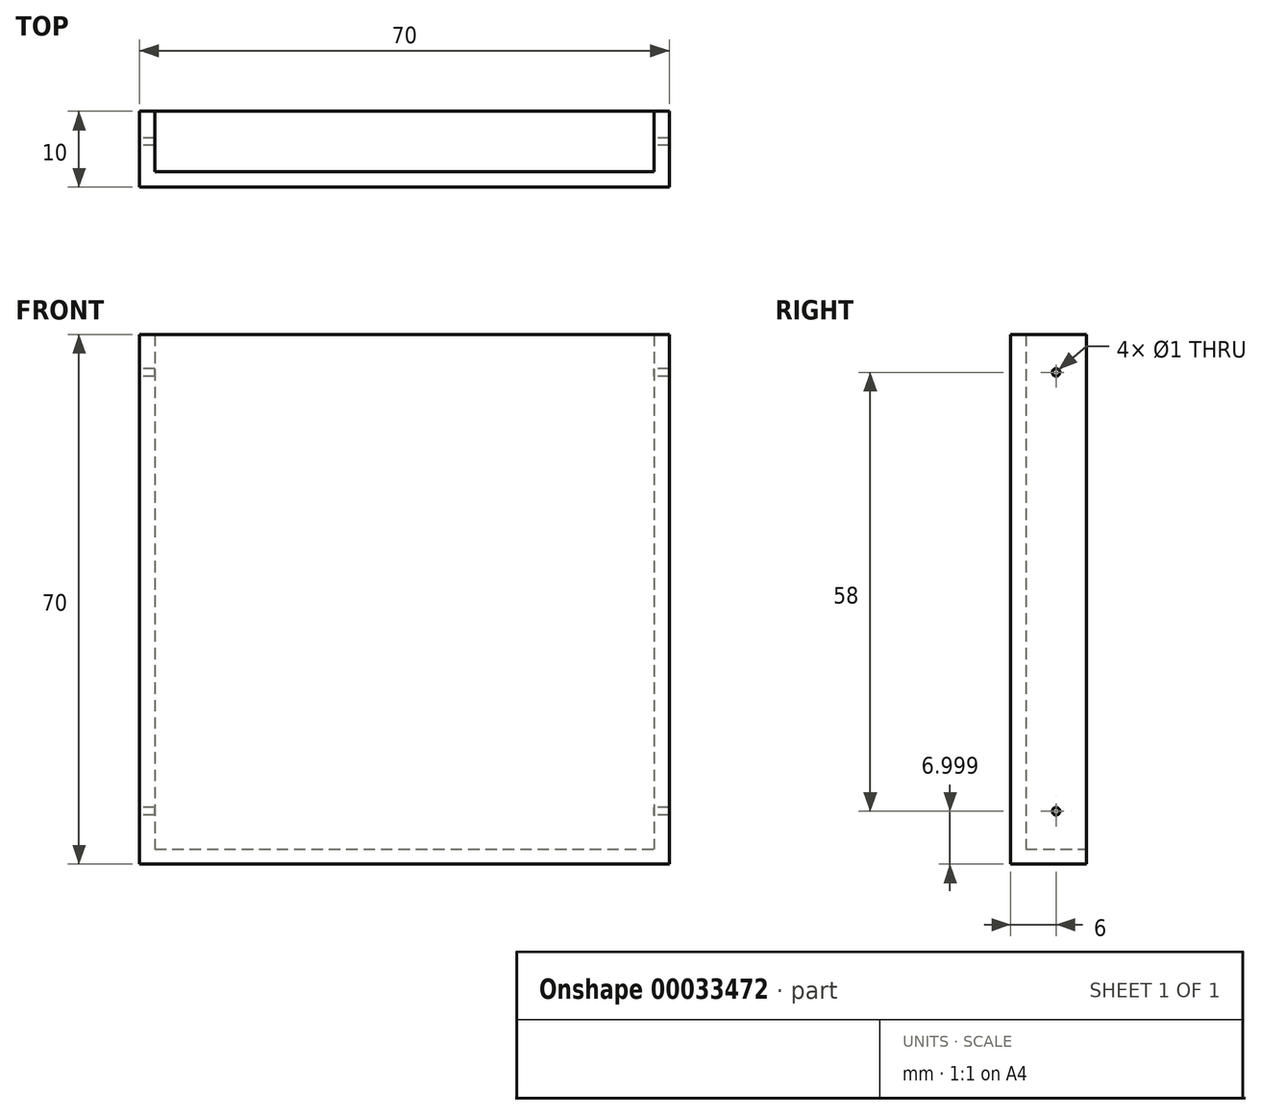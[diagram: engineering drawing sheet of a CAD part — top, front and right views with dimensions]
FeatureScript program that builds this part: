
annotation { "Feature Type Name" : "Feature", "Feature Type Description" : "" }
export const myFeature = defineFeature(function(context is Context, id is Id, definition is map)
    precondition{}
    {
        {
            var Q0;
            Q0=qCreatedBy(makeId("Front.planeOp"),FACE);
            var sketch = newSketch(context, id + "F0", { "sketchPlane" : qUnion([Q0])});
            skLineSegment(sketch, "E0.bottom", {"start": v(-35, 27.79) * mm, "end": v(35, 27.79) * mm});
            skLineSegment(sketch, "E0.top", {"start": v(-35, -42.21) * mm, "end": v(35, -42.21) * mm});
            skLineSegment(sketch, "E0.left", {"start": v(-35, 27.79) * mm, "end": v(-35, -42.21) * mm});
            skLineSegment(sketch, "E0.right", {"start": v(35, 27.79) * mm, "end": v(35, -42.21) * mm});
            skLineSegment(sketch, "E1", {"start": v(0, 0) * mm, "end": v(0, 74.16) * mm, "construction": true});
            skSolve(sketch);
        }
        {
            var Q0;
            Q0=makeQuery(id+"F0.imprint","IMPRINT",FACE,{"disambiguationData":[TD([[makeQuery(id+"F0.imprint","IMPRINT",EDGE,{"derivedFrom":sQuery(id+"F0.wireOp",EDGE,"E0.bottom")}),-1.0]])]});
            extrude(context, id + "F1", {"entities" : qUnion([Q0]), "depth" : 10 * mm});
        }
        {
            var Q0;
            Q0=makeQuery(id+"F1.opExtrude","CAP_FACE",FACE,{"disambiguationData":[OSD([sQuery(id+"F0.wireOp",EDGE,"E0.bottom"),sQuery(id+"F0.wireOp",EDGE,"E0.top"),sQuery(id+"F0.wireOp",EDGE,"E0.left"),sQuery(id+"F0.wireOp",EDGE,"E0.right")])],"isStart":true});
            shell(context, id + "F2", {"entities" : qUnion([Q0]), "thickness" : 2 * mm});
        }
        {
            var Q0;
            Q0=makeQuery(id+"F1.opExtrude","SWEPT_FACE",FACE,{"disambiguationData":[OSD([sQuery(id+"F0.wireOp",EDGE,"E0.bottom")])]});
            var sketch = newSketch(context, id + "F3", { "sketchPlane" : qUnion([Q0])});
            skLineSegment(sketch, "E2", {"start": v(-33, 0) * mm, "end": v(-33, -8) * mm});
            skLineSegment(sketch, "E3", {"start": v(-33, -8) * mm, "end": v(33, -8) * mm});
            skLineSegment(sketch, "E4", {"start": v(33, -8) * mm, "end": v(33, 0) * mm});
            skSolve(sketch);
        }
        {
            var Q0;
            {var subQ2=sQuery(id+"F3.wireOp",EDGE,"E2");Q0=makeQuery(id+"F3.imprint","IMPRINT",FACE,{"disambiguationData":[TD([[makeQuery(id+"F3.imprint","IMPRINT",EDGE,{"derivedFrom":subQ2}),1.0]])]});}
            extrude(context, id + "F4", {"entities" : qUnion([Q0]), "operationType" : NewBodyOperationType.REMOVE, "oppositeDirection" : true, "depth" : 4.33 * mm});
        }
        {
            var Q0;
            Q0=makeQuery(id+"F4.boolean.opBoolean","MERGE",FACE,{"derivedFrom":[makeQuery(id+"F2.opShell","OFFSET_FACE",FACE,{"disambiguationData":[OSD([sQuery(id+"F0.wireOp",EDGE,"E0.right")])]}),makeQuery(id+"F4.opExtrude","SWEPT_FACE",FACE,{"disambiguationData":[OSD([sQuery(id+"F3.wireOp",EDGE,"E4")])]})]});
            var sketch = newSketch(context, id + "F5", { "sketchPlane" : qUnion([Q0])});
            skCircle(sketch, "E5", {"center": v(4, 22.79) * mm, "radius": 0.5 * mm});
            skCircle(sketch, "E6", {"center": v(4, -35.21) * mm, "radius": 0.5 * mm});
            skLineSegment(sketch, "E7", {"start": v(4, 27.79) * mm, "end": v(4, -40.21) * mm, "construction": true});
            skSolve(sketch);
        }
        {
            var Q0;
            Q0=makeQuery(id+"F5.imprint","IMPRINT",FACE,{"disambiguationData":[TD([[makeQuery(id+"F5.imprint","IMPRINT",EDGE,{"derivedFrom":sQuery(id+"F5.wireOp",EDGE,"E5")}),1.0]])]});
            var Q1;
            Q1=makeQuery(id+"F5.imprint","IMPRINT",FACE,{"disambiguationData":[TD([[makeQuery(id+"F5.imprint","IMPRINT",EDGE,{"derivedFrom":sQuery(id+"F5.wireOp",EDGE,"E6")}),1.0]])]});
            extrude(context, id + "F6", {"entities" : qUnion([Q0, Q1]), "operationType" : NewBodyOperationType.REMOVE, "endBound" : BoundingType.THROUGH_ALL, "oppositeDirection" : true, "depth" : 25 * mm, "hasSecondDirection" : true, "secondDirectionBound" : SecondDirectionBoundingType.THROUGH_ALL, "secondDirectionOppositeDirection" : false, "secondDirectionDepth" : 25 * mm});
        }
    });
